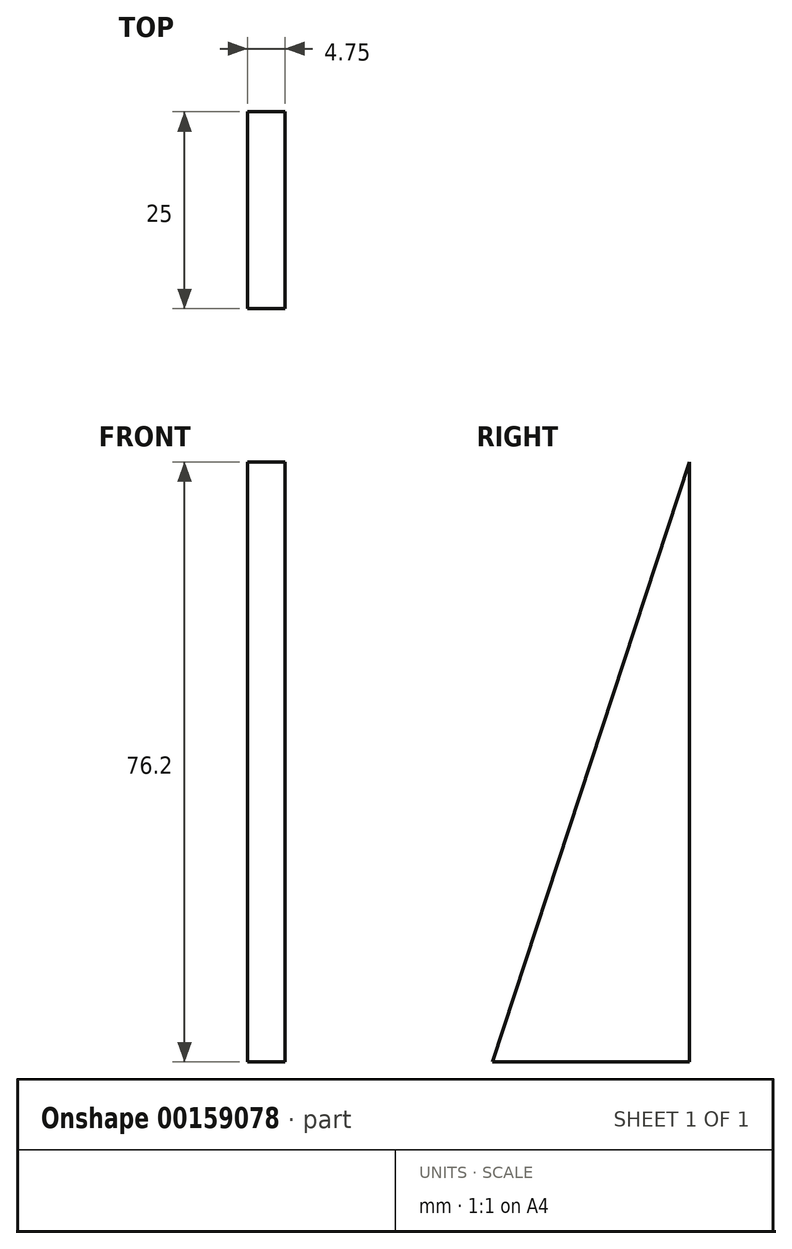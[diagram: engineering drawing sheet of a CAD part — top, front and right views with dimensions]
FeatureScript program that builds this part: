
annotation { "Feature Type Name" : "Feature", "Feature Type Description" : "" }
export const myFeature = defineFeature(function(context is Context, id is Id, definition is map)
    precondition{}
    {
        {
            var Q0;
            Q0=qCreatedBy(makeId("Right.planeOp"),FACE);
            var sketch = newSketch(context, id + "F0", { "sketchPlane" : qUnion([Q0])});
            skLineSegment(sketch, "E0", {"start": v(-11.65, -14.79) * mm, "end": v(13.35, -14.79) * mm});
            skLineSegment(sketch, "E1", {"start": v(13.35, -14.79) * mm, "end": v(13.35, 61.41) * mm});
            skLineSegment(sketch, "E2", {"start": v(13.35, 61.41) * mm, "end": v(-11.65, -14.79) * mm});
            skSolve(sketch);
        }
        {
            var Q0;
            Q0 = qSketchRegion(id + "F0", true);
            extrude(context, id + "F1", {"entities" : qUnion([Q0]), "depth" : 4.75 * mm});
        }
    });
